# Revit family: Chair-Hussey-Quattro-Art_Series-Linear-3D-Metric
name_source: partatom
category: Furniture
units: mm (PartAtom-declared; Revit-internal decimal feet)

## family parameters
Always vertical = Yes
Cut with Voids When Loaded = No
OmniClass Number = 23.40.50.11.11.11
OmniClass Title = Fixed Audience Seating
Room Calculation Point = No
Shared = No
Work Plane-Based = No

## types (1)
- Chair-Hussey-Quattro-Art_Series-Linear-3D-Metric
    3D Configurator = https://www.husseyseating.com
    Armrest Finish = Hussey - Wood - Grasswood - Natural Finish
    Assembly Code = E2010500
    BIM Version = v3.2
    BIM Version Available (Earliest) = 2017
    CSI MasterFormat = 12 61 00
    Default Elevation = 0 mm
    Description = Quattro Art Series
    Designer Guide = Refer to Product Selector Worksheet for all Options
    End Panel Finish = Hussey - Wood - Grasswood - Natural Finish
    Finish Options Website Link = http://204.239.146.105
    Floor Slope Angle = 0.00°
    Manufacturer = Hussey Seating Company
    Model = Quattro Art Series
    Product Brochure PDF = http://www.hscedocs.com
    Product Page URL = https://www.husseyseating.com
    Product Selector Worksheet Link = http://hscedocs.com
    Quattro Literature Downloads = http://www.husseyseating.com
    Seat Back Angle = 18.00°
    Seat Back Angle Note = 12°, 15°, 18° or 21°
    Seat Back Finish = Hussey - Fabric - Culp Contract - Dillon - Cordovan
    Seat Back Outer Finish = Hussey - Wood - Grasswood - Natural Finish
    Seat Bottom Cover Finish = Hussey - Wood - Grasswood - Natural Finish
    Seat Pad Finish = Hussey - Fabric - Culp Contract - Dillon - Cordovan
    Seat Width Note = 500 mm, 525 mm, 550 mm, 575 mm, or 600 mm
    Series = Art Series - Linear
    Stanchion Finish = Hussey - Paint - Titanium
    URL = http://www.husseyseating.com

## geometry (parser evidence)
native form markers: Extrusion x2, Sweep x12
no freeform markers — native parametric forms only
